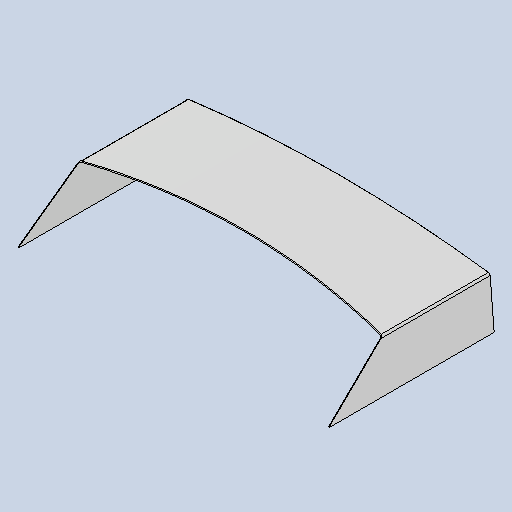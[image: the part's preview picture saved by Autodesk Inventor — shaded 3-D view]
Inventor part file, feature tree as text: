
AUTODESK INVENTOR PART (.ipt)
format: ipt  version: 2025 (Build 290162010, 162A)  size: 315,392 bytes
history: native  units: mm
features: other x4, sheet_metal_op x3, sketch x3, mirror x1, extrude x1, fillet x1
ambient origin geometry x8: Origin, YZ Plane, XZ Plane, XY Plane, X Axis, Y Axis, Z Axis, Center Point
bodies: Body1 (feature_tree)
feature tree (13):
  sheet_metal_op  "Contour Flange2"
  mirror  "Mirror2"
  extrude  "Extrusion2"  Depth=3.0mm
  fillet  "Fillet1"  Radius=1.5mm
  other  "Mark2"
  other  "A-Side Definition"
  sketch  "Sketch1"  dims[d36=3.0mm d37=3.0mm d38=1.5mm]
  other  "Plate2"
  sheet_metal_op  "Bend2"
  sheet_metal_op  "Corner2"
  sketch  "Sketch2"  dims[d39=6.0mm]
  sketch  "Sketch4"  dims[d40=3.0mm d41=819.0mm d42=3.0mm d43=3.0mm d44=12.0mm d45=3.0mm d46=3.0mm d65=6.0mm d78=3.0mm d80=3.0mm d123=0.0mm d124=0.0mm d128=2.0mm d134=1500.0mm d135=2700.0mm d136=2100.0mm d137=8.0mm d138=50.0mm d139=50.0mm d140=3.0mm d141=10.0mm d142=241.9mm d146=3.0mm d148=5.0mm d149=6.981317mm d150=500.0mm]
  other  "Definition1"
